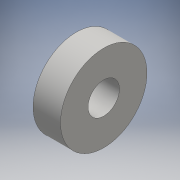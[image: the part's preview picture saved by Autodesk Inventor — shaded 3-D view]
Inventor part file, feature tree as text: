
AUTODESK INVENTOR PART (.ipt)
format: ipt  version: 2016 (Build 200138000, 138)  size: 104,448 bytes
history: native  units: mm
features: extrude x1, plane x1, sketch x1
ambient origin geometry x8: Origin, YZ Plane, XZ Plane, XY Plane, X Axis, Y Axis, Z Axis, Center Point
bodies: Solid1 (feature_tree)
feature tree (3):
  extrude  "Extrusion1"  Depth=7.0mm
  plane  "Work Plane1"
  sketch  "Sketch1"  dims[d0=8.0mm d1=22.0mm d2=7.0mm d3=0.0mm d4=-3.5mm]
